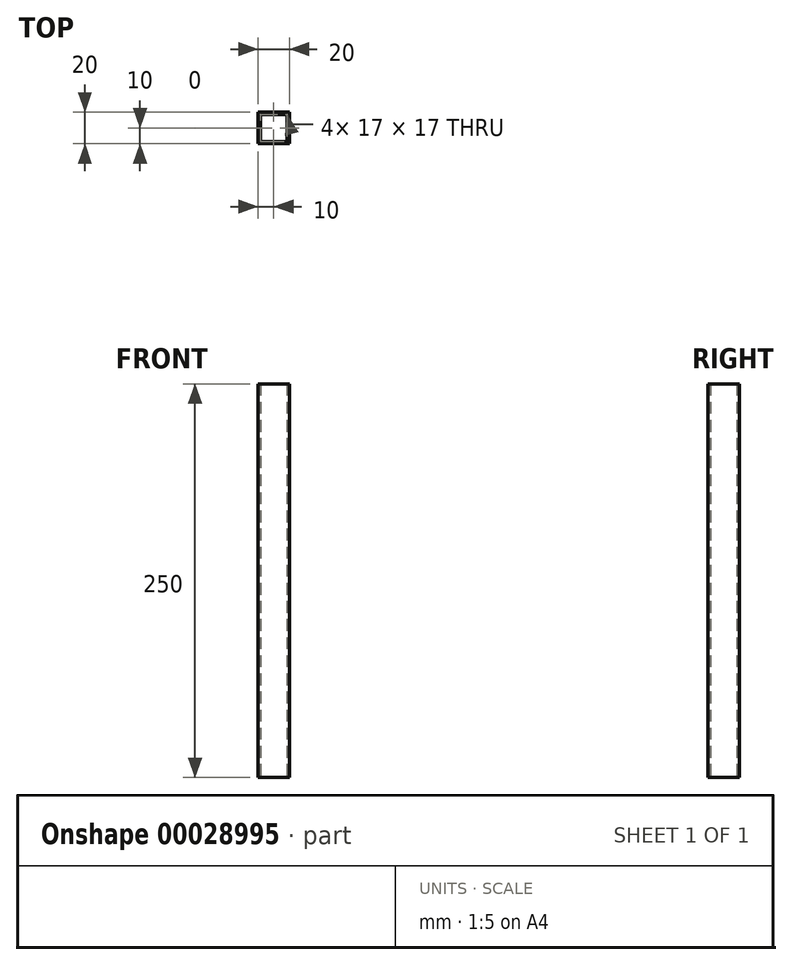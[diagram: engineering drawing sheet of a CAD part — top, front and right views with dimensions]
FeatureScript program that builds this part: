
annotation { "Feature Type Name" : "Feature", "Feature Type Description" : "" }
export const myFeature = defineFeature(function(context is Context, id is Id, definition is map)
    precondition{}
    {
        {
            var Q0;
            Q0=qCreatedBy(makeId("Top.planeOp"),FACE);
            var sketch = newSketch(context, id + "F0", { "sketchPlane" : qUnion([Q0])});
            skLineSegment(sketch, "E0.rect.bottom", {"start": v(8.5, -8.5) * mm, "end": v(-8.5, -8.5) * mm});
            skLineSegment(sketch, "E0.rect.top", {"start": v(8.5, 8.5) * mm, "end": v(-8.5, 8.5) * mm});
            skLineSegment(sketch, "E0.rect.left", {"start": v(8.5, -8.5) * mm, "end": v(8.5, 8.5) * mm});
            skLineSegment(sketch, "E0.rect.right", {"start": v(-8.5, -8.5) * mm, "end": v(-8.5, 8.5) * mm});
            skPoint(sketch, "E0.rect.middle", {"position": v(0, 0) * mm});
            skLineSegment(sketch, "E1.rect.bottom", {"start": v(10, -10) * mm, "end": v(-10, -10) * mm});
            skLineSegment(sketch, "E1.rect.top", {"start": v(10, 10) * mm, "end": v(-10, 10) * mm});
            skLineSegment(sketch, "E1.rect.left", {"start": v(10, -10) * mm, "end": v(10, 10) * mm});
            skLineSegment(sketch, "E1.rect.right", {"start": v(-10, -10) * mm, "end": v(-10, 10) * mm});
            skSolve(sketch);
        }
        {
            var Q0;
            Q0 = qSketchRegion(id + "F0", true);
            extrude(context, id + "F1", {"entities" : qUnion([Q0]), "depth" : 250 * mm});
        }
    });
